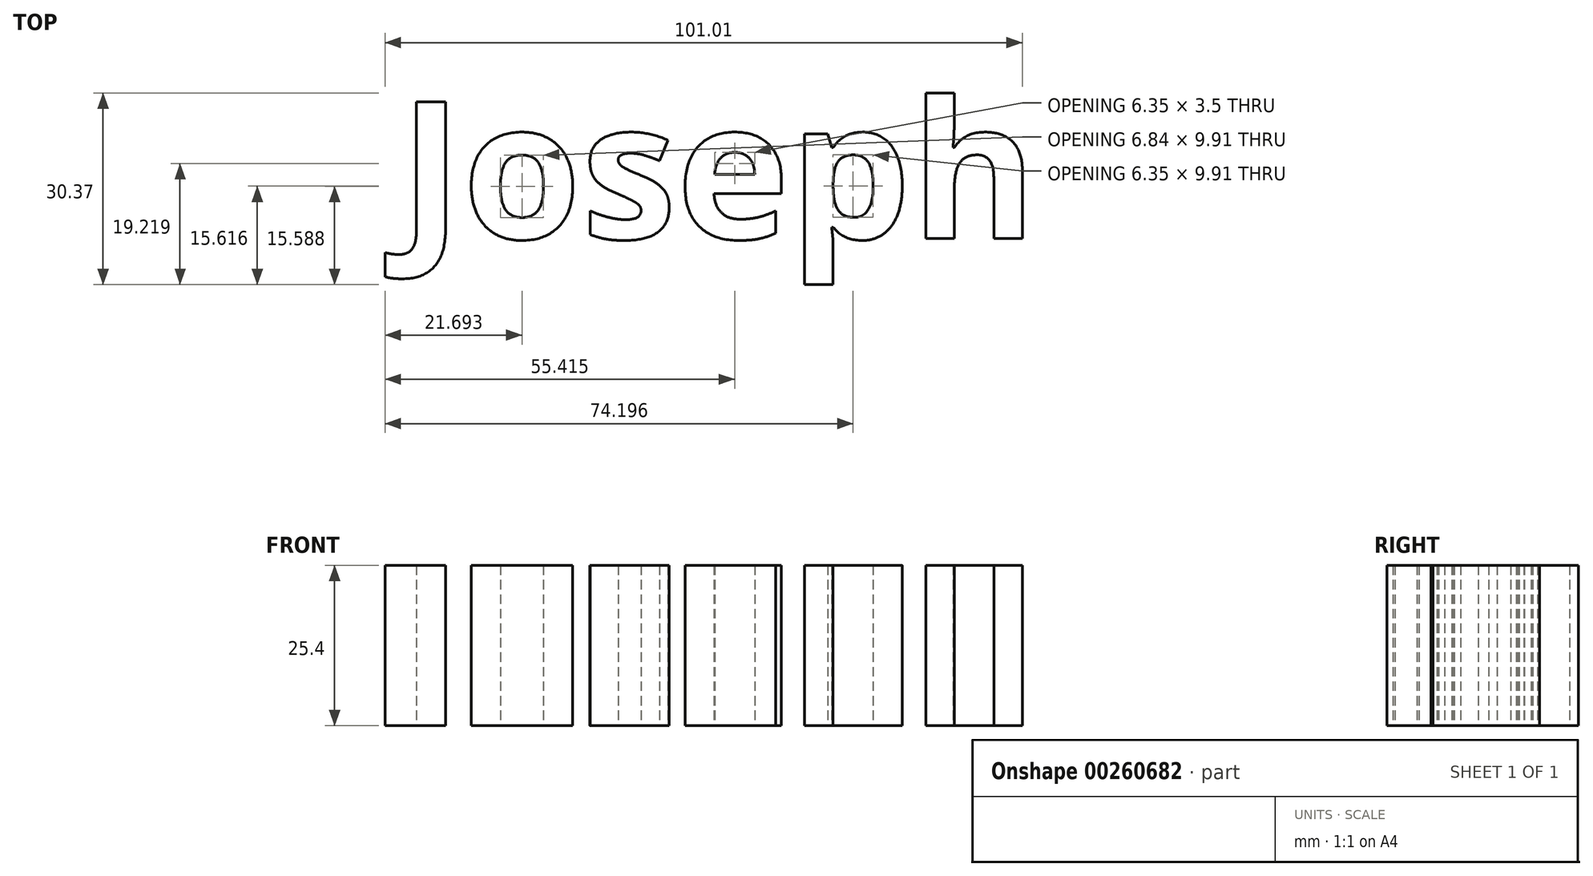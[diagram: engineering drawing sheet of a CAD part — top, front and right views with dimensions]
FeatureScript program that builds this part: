
annotation { "Feature Type Name" : "Feature", "Feature Type Description" : "" }
export const myFeature = defineFeature(function(context is Context, id is Id, definition is map)
    precondition{}
    {
        {
            var Q0;
            Q0=qCreatedBy(makeId("Top.planeOp"),FACE);
            var sketch = newSketch(context, id + "F0", { "sketchPlane" : qUnion([Q0])});
            skText(sketch, "E0", { "text": "Joseph \n", "fontName": "OpenSans-Bold.ttf"});
            const initialGuessF0  = {"E0": [-0.04256, 0.02696, 1, 0, 0.02186]};
            skSetInitialGuess(sketch, initialGuessF0);
            skSolve(sketch);
        }
        {
            var Q0;
            Q0 = qSketchRegion(id + "F0", true);
            extrude(context, id + "F1", {"entities" : qUnion([Q0]), "depth" : 25.4 * mm});
        }
    });
